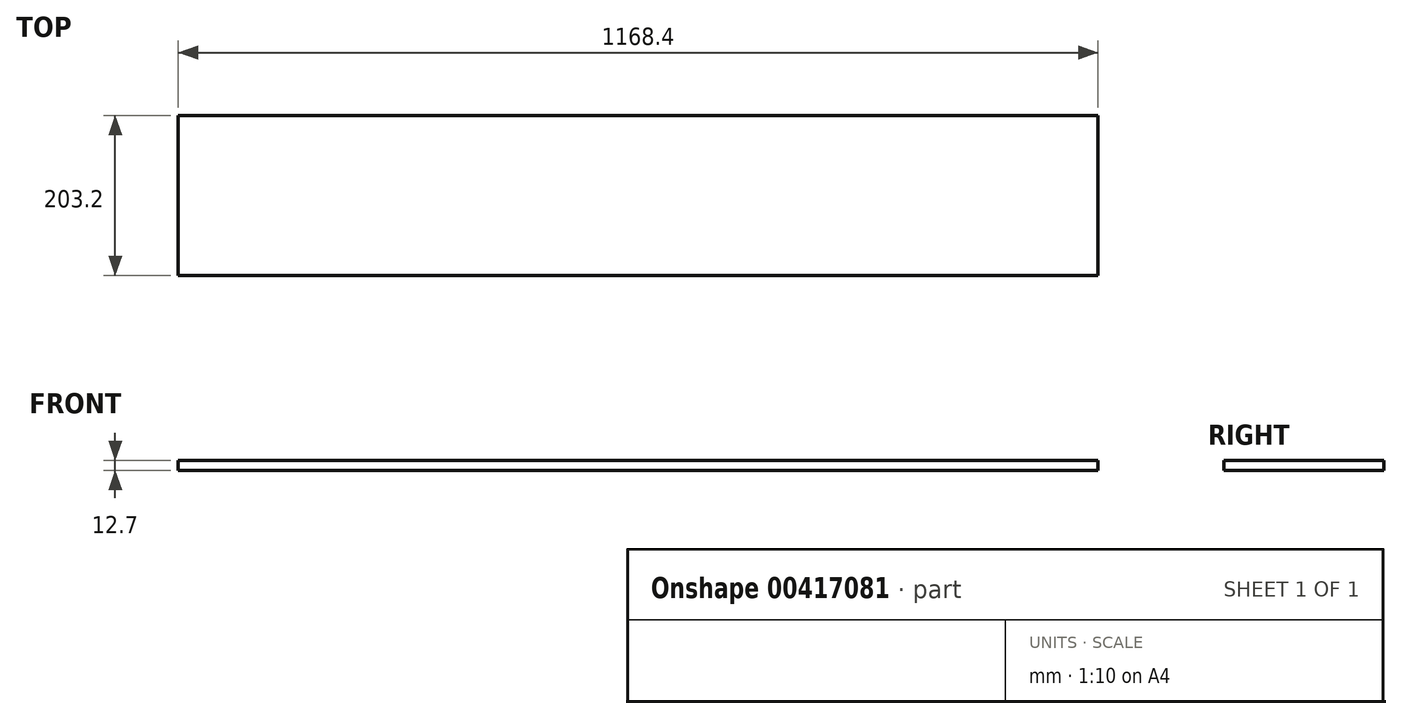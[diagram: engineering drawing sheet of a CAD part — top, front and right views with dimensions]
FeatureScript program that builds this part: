
annotation { "Feature Type Name" : "Feature", "Feature Type Description" : "" }
export const myFeature = defineFeature(function(context is Context, id is Id, definition is map)
    precondition{}
    {
        {
            var Q0;
            Q0=qCreatedBy(makeId("Top.planeOp"),FACE);
            var sketch = newSketch(context, id + "F0", { "sketchPlane" : qUnion([Q0])});
            skLineSegment(sketch, "E0.bottom", {"start": v(-584.2, 0) * mm, "end": v(584.2, 0) * mm});
            skLineSegment(sketch, "E0.top", {"start": v(-584.2, -203.2) * mm, "end": v(584.2, -203.2) * mm});
            skLineSegment(sketch, "E0.left", {"start": v(-584.2, 0) * mm, "end": v(-584.2, -203.2) * mm});
            skLineSegment(sketch, "E0.right", {"start": v(584.2, 0) * mm, "end": v(584.2, -203.2) * mm});
            skLineSegment(sketch, "E1", {"start": v(0, 0) * mm, "end": v(0, -203.2) * mm, "construction": true});
            skSolve(sketch);
        }
        {
            var Q0;
            Q0 = qSketchRegion(id + "F0", true);
            extrude(context, id + "F1", {"entities" : qUnion([Q0]), "depth" : 12.7 * mm});
        }
    });
